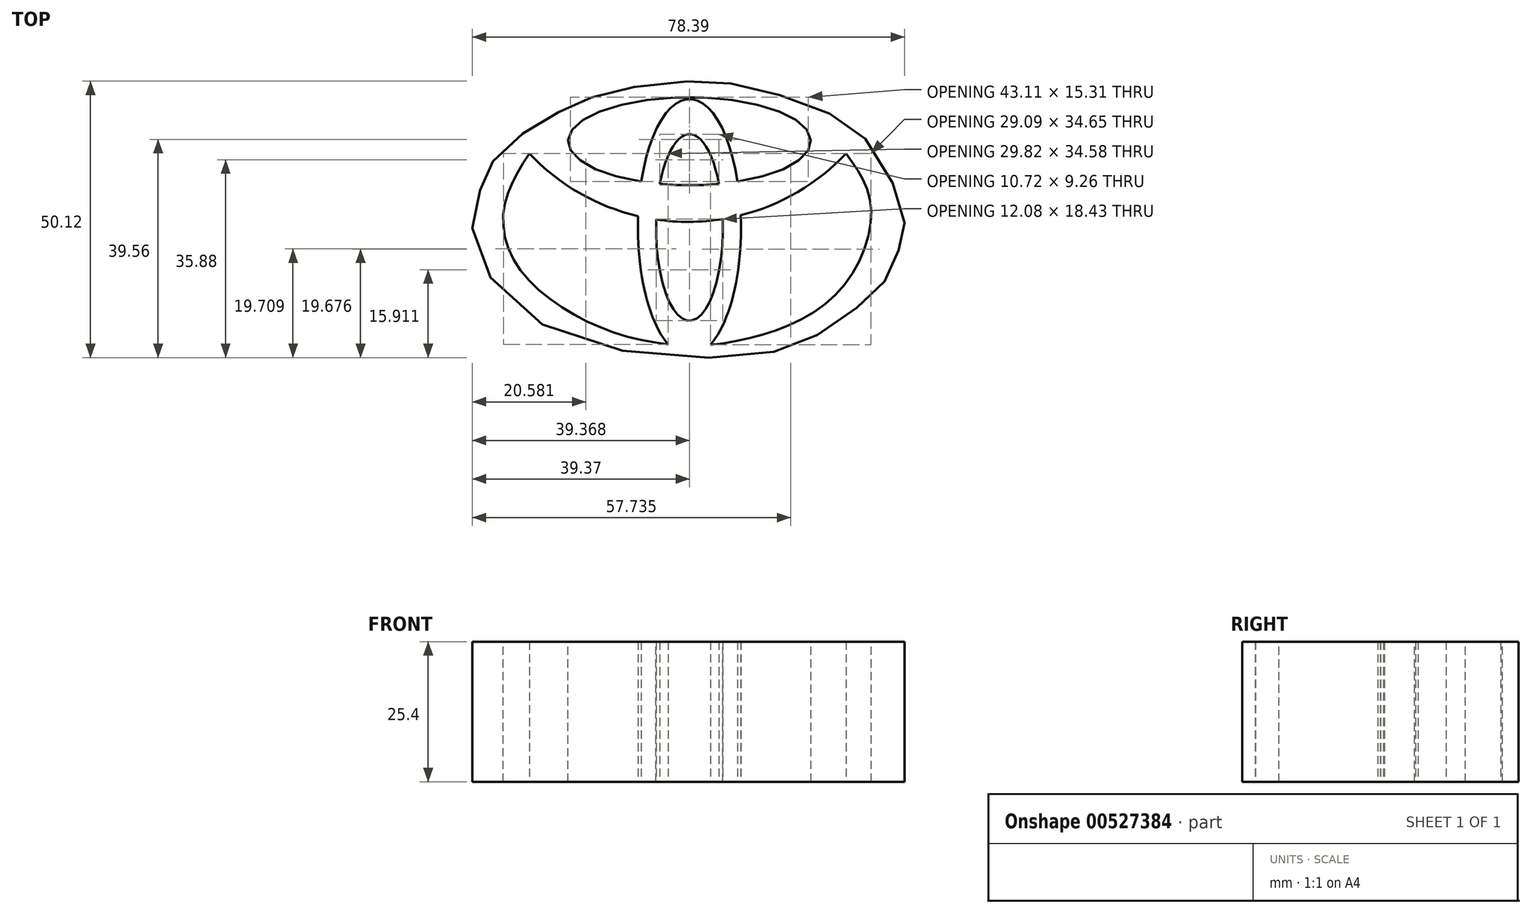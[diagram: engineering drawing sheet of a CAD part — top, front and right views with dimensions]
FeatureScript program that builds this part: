
annotation { "Feature Type Name" : "Feature", "Feature Type Description" : "" }
export const myFeature = defineFeature(function(context is Context, id is Id, definition is map)
    precondition{}
    {
        {
            var Q0;
            Q0=qCreatedBy(makeId("Top.planeOp"),FACE);
            var sketch = newSketch(context, id + "F0", { "sketchPlane" : qUnion([Q0])});
            skFitSpline(sketch, "E0", {"points": [v(-37.96, 2.54) * mm, v(-35.73, 7.64) * mm, v(-29.03, 13.7) * mm, v(-21.37, 17.85) * mm, v(-14.35, 20.4) * mm, v(0, 22.32) * mm, v(10.53, 21.36) * mm, v(25.2, 16.58) * mm, v(33.5, 9.88) * mm, v(38.92, -2.24) * mm, v(38.6, -5.75) * mm, v(36.69, -11.81) * mm, v(32.86, -16.6) * mm, v(23.29, -23.62) * mm, v(10.2, -27.44) * mm, v(-26.16, -22.02) * mm, v(-39.24, -5.75) * mm, v(-37.96, 2.54) * mm]});
            skEllipse(sketch, "E1", {"center": v(0, 11.47) * mm, "majorRadius": 22.01 * mm, "minorRadius": 7.98 * mm, "majorAxis": v(1, 0)});
            skEllipse(sketch, "E2", {"center": v(0, -4.16) * mm, "majorRadius": 16.9 * mm, "minorRadius": 6.06 * mm, "majorAxis": v(0, 1)});
            skEllipse(sketch, "E3", {"center": v(0, -4.16) * mm, "majorRadius": 23.29 * mm, "minorRadius": 9.34 * mm, "majorAxis": v(0, 1)});
            skArc(sketch, "E4", {"start": v(-29.03, 9.24) * mm, "mid": v(-0.32, -3.15) * mm, "end": v(28.4, 9.24) * mm});
            skFitSpline(sketch, "E5", {"points": [v(-29.03, 9.24) * mm, v(-33.5, 0) * mm, v(-31.58, -10.54) * mm, v(-19.46, -20.75) * mm, v(-3.9, -25.34) * mm, v(12.12, -23.94) * mm, v(27.75, -15) * mm, v(32.86, 0) * mm, v(28.4, 9.24) * mm], "startDerivative": vector(-53, -82.97) * mm, "endDerivative": vector(-56.63, 77.57) * mm});
            skSolve(sketch);
        }
        {
            var Q0;
            Q0=makeQuery(id+"F0.imprint","IMPRINT",FACE,{"disambiguationData":[TD([[makeQuery(id+"F0.imprint","IMPRINT",EDGE,{"derivedFrom":sQuery(id+"F0.wireOp",EDGE,"E0")}),-1.0]])]});
            var Q1;
            {var subQ0=sQuery(id+"F0.wireOp",EDGE,"E2");var subQ1=sQuery(id+"F0.wireOp",EDGE,"E1");var subQ2=makeQuery(id+"F0.imprint","INTERSECT",VERTEX,{"disambiguationData":[OD(0.0)],"derivedFrom":[subQ1,subQ0]});Q1=makeQuery(id+"F0.imprint","IMPRINT",FACE,{"disambiguationData":[TD([[makeQuery(id+"F0.imprint","IMPRINT",EDGE,{"disambiguationData":[TD([[subQ2,1.0]])],"derivedFrom":subQ1}),1.0]])]});}
            var Q2;
            {var subQ0=sQuery(id+"F0.wireOp",EDGE,"E2");var subQ1=sQuery(id+"F0.wireOp",EDGE,"E1");var subQ2=makeQuery(id+"F0.imprint","INTERSECT",VERTEX,{"disambiguationData":[OD(0.0)],"derivedFrom":[subQ1,subQ0]});Q2=makeQuery(id+"F0.imprint","IMPRINT",FACE,{"disambiguationData":[TD([[makeQuery(id+"F0.imprint","IMPRINT",EDGE,{"disambiguationData":[TD([[subQ2,1.0]])],"derivedFrom":subQ1}),-1.0]])]});}
            var Q3;
            {var subQ0=sQuery(id+"F0.wireOp",EDGE,"E2");var subQ1=sQuery(id+"F0.wireOp",EDGE,"E1");var subQ2=makeQuery(id+"F0.imprint","INTERSECT",VERTEX,{"disambiguationData":[OD(0.0)],"derivedFrom":[subQ1,subQ0]});Q3=makeQuery(id+"F0.imprint","IMPRINT",FACE,{"disambiguationData":[TD([[makeQuery(id+"F0.imprint","IMPRINT",EDGE,{"disambiguationData":[TD([[subQ2,-1.0]])],"derivedFrom":subQ1}),-1.0]])]});}
            var Q4;
            {var subQ0=sQuery(id+"F0.wireOp",EDGE,"E2");var subQ1=sQuery(id+"F0.wireOp",EDGE,"E1");var subQ2=makeQuery(id+"F0.imprint","INTERSECT",VERTEX,{"disambiguationData":[OD(1.0)],"derivedFrom":[subQ1,subQ0]});Q4=makeQuery(id+"F0.imprint","IMPRINT",FACE,{"disambiguationData":[TD([[makeQuery(id+"F0.imprint","IMPRINT",EDGE,{"disambiguationData":[TD([[subQ2,-1.0]])],"derivedFrom":subQ1}),-1.0]])]});}
            var Q5;
            {var subQ3=sQuery(id+"F0.wireOp",EDGE,"E4");var subQ7=sQuery(id+"F0.wireOp",EDGE,"E2");var subQ8=makeQuery(id+"F0.imprint","INTERSECT",VERTEX,{"disambiguationData":[OD(0.0)],"derivedFrom":[subQ7,subQ3]});Q5=makeQuery(id+"F0.imprint","IMPRINT",FACE,{"disambiguationData":[TD([[makeQuery(id+"F0.imprint","IMPRINT",EDGE,{"disambiguationData":[TD([[subQ8,-1.0]])],"derivedFrom":subQ7}),-1.0]])]});}
            var Q6;
            {var subQ0=sQuery(id+"F0.wireOp",EDGE,"E5");var subQ1=sQuery(id+"F0.wireOp",EDGE,"E3");var subQ2=makeQuery(id+"F0.imprint","INTERSECT",VERTEX,{"disambiguationData":[OD(0.0)],"derivedFrom":[subQ1,subQ0]});Q6=makeQuery(id+"F0.imprint","IMPRINT",FACE,{"disambiguationData":[TD([[makeQuery(id+"F0.imprint","IMPRINT",EDGE,{"disambiguationData":[TD([[subQ2,-1.0]])],"derivedFrom":subQ1}),1.0]])]});}
            extrude(context, id + "F1", {"entities" : qUnion([Q0, Q1, Q2, Q3, Q4, Q5, Q6]), "depth" : 25.4 * mm, "offsetDistance" : 25.4 * mm});
        }
    });
